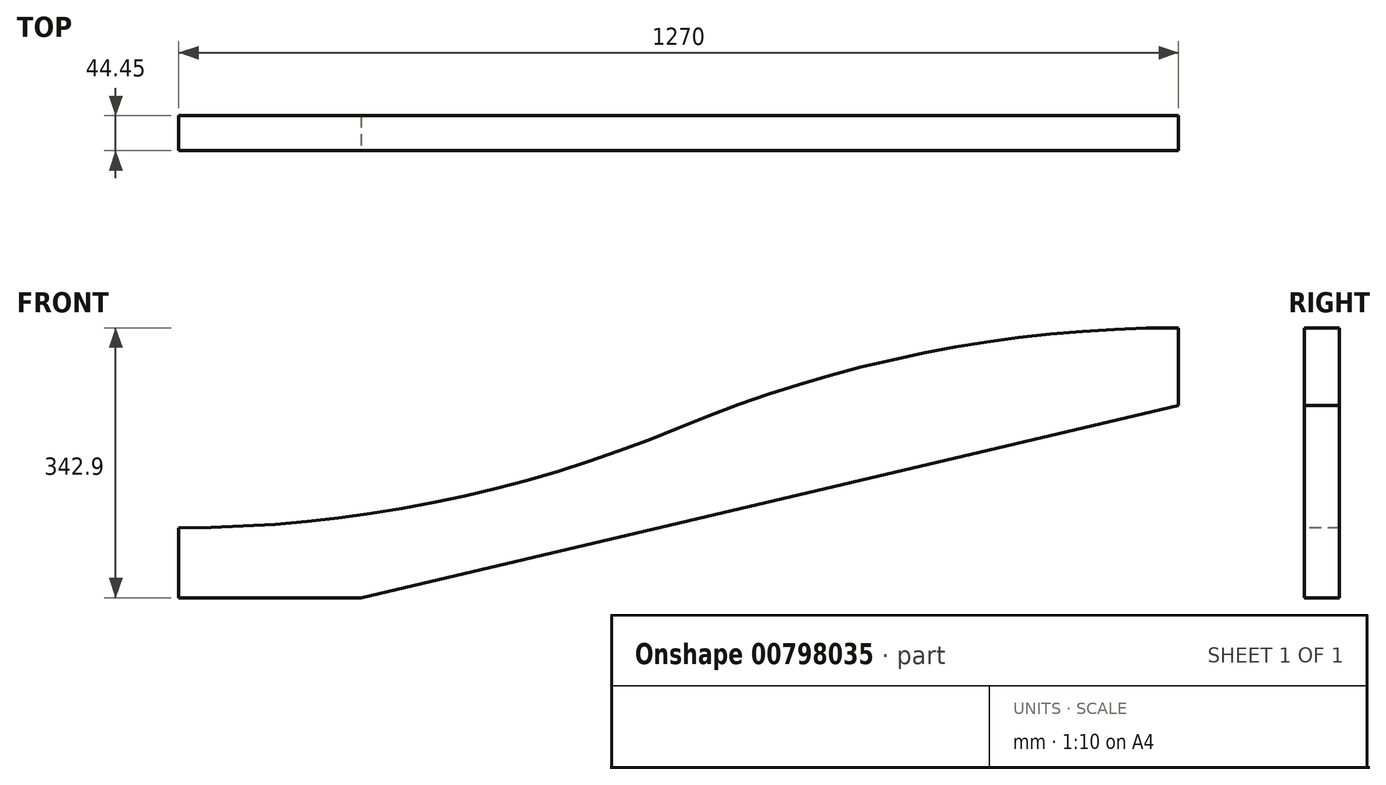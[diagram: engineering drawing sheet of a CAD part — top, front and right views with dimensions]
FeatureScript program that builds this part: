
annotation { "Feature Type Name" : "Feature", "Feature Type Description" : "" }
export const myFeature = defineFeature(function(context is Context, id is Id, definition is map)
    precondition{}
    {
        {
            var Q0;
            Q0=qCreatedBy(makeId("Front.planeOp"),FACE);
            var sketch = newSketch(context, id + "F0", { "sketchPlane" : qUnion([Q0])});
            skLineSegment(sketch, "E0.bottom", {"start": v(0, 0) * mm, "end": v(1270, 0) * mm});
            skLineSegment(sketch, "E0.top", {"start": v(0, 342.9) * mm, "end": v(1270, 342.9) * mm});
            skLineSegment(sketch, "E0.left", {"start": v(0, 0) * mm, "end": v(0, 342.9) * mm});
            skLineSegment(sketch, "E0.right", {"start": v(1270, 0) * mm, "end": v(1270, 342.9) * mm});
            skLineSegment(sketch, "E1", {"start": v(0, 88.9) * mm, "end": v(1270, 88.9) * mm});
            skArc(sketch, "E2", {"start": v(0, 88.9) * mm, "mid": v(323.79, 120.96) * mm, "end": v(635, 215.9) * mm});
            skArc(sketch, "E3", {"start": v(1270, 342.9) * mm, "mid": v(946.21, 310.84) * mm, "end": v(635, 215.9) * mm});
            skLineSegment(sketch, "E4", {"start": v(0, 88.9) * mm, "end": v(1270, 388.1) * mm});
            skLineSegment(sketch, "E5", {"start": v(0, -54.62) * mm, "end": v(1270, 244.57) * mm});
            skLineSegment(sketch, "E6", {"start": v(1270, 388.1) * mm, "end": v(1270, 244.57) * mm});
            skLineSegment(sketch, "E7", {"start": v(0, 88.9) * mm, "end": v(0, -54.62) * mm});
            skSolve(sketch);
        }
        {
            var Q0;
            {var subQ1=sQuery(id+"F0.wireOp",EDGE,"E2");Q0=makeQuery(id+"F0.imprint","IMPRINT",FACE,{"disambiguationData":[TD([[makeQuery(id+"F0.imprint","IMPRINT",EDGE,{"derivedFrom":subQ1}),-1.0]])]});}
            var Q1;
            {var subQ0=sQuery(id+"F0.wireOp",EDGE,"E7");var subQ1=sQuery(id+"F0.wireOp",EDGE,"E0.bottom");var subQ2=makeQuery(id+"F0.imprint","INTERSECT",VERTEX,{"derivedFrom":[subQ1,subQ0]});Q1=makeQuery(id+"F0.imprint","IMPRINT",FACE,{"disambiguationData":[TD([[makeQuery(id+"F0.imprint","IMPRINT",EDGE,{"disambiguationData":[TD([[subQ2,-1.0]])],"derivedFrom":subQ1}),1.0]])]});}
            extrude(context, id + "F1", {"entities" : qUnion([Q0, Q1]), "oppositeDirection" : true, "depth" : 44.45 * mm, "offsetDistance" : 25.4 * mm});
        }
    });
